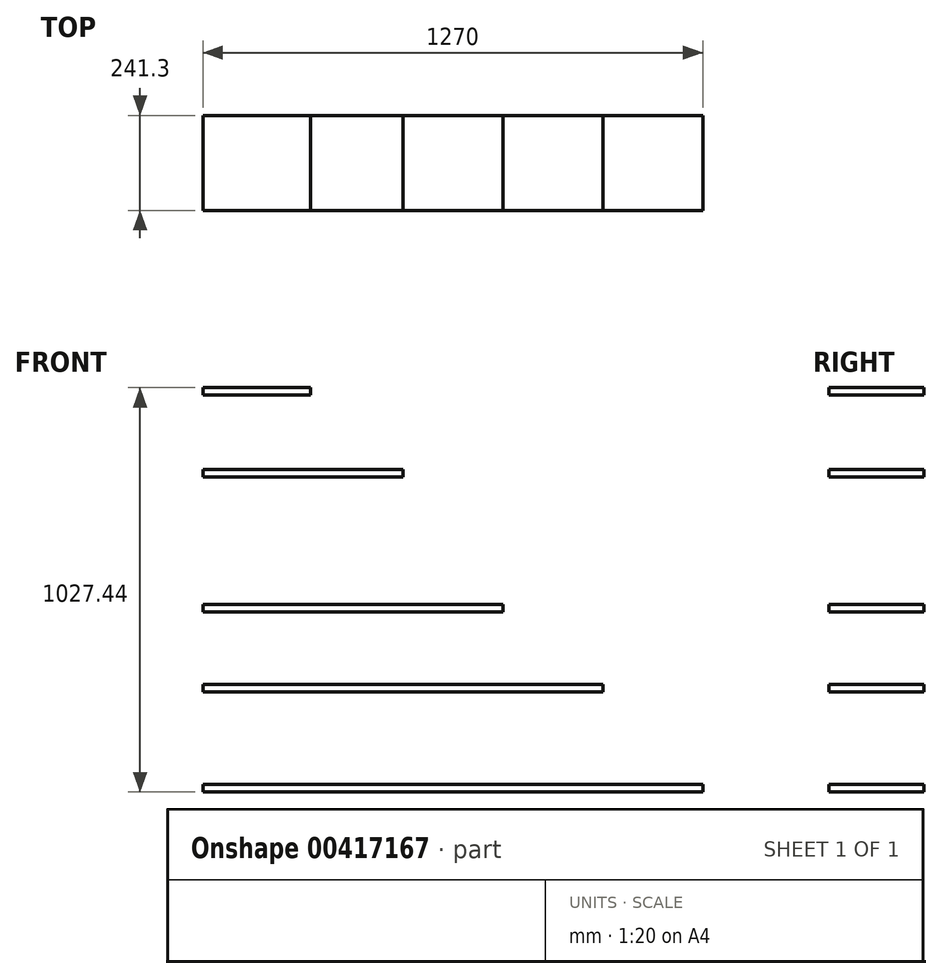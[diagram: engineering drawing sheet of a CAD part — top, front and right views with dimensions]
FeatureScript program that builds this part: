
annotation { "Feature Type Name" : "Feature", "Feature Type Description" : "" }
export const myFeature = defineFeature(function(context is Context, id is Id, definition is map)
    precondition{}
    {
        {
            var Q0;
            Q0=qCreatedBy(makeId("Front.planeOp"),FACE);
            var sketch = newSketch(context, id + "F0", { "sketchPlane" : qUnion([Q0])});
            skLineSegment(sketch, "E0.bottom", {"start": v(635, 9.52) * mm, "end": v(-635, 9.52) * mm});
            skLineSegment(sketch, "E0.top", {"start": v(635, -9.53) * mm, "end": v(-635, -9.53) * mm});
            skLineSegment(sketch, "E0.left", {"start": v(635, 9.52) * mm, "end": v(635, -9.53) * mm});
            skLineSegment(sketch, "E0.right", {"start": v(-635, 9.52) * mm, "end": v(-635, -9.53) * mm});
            skPoint(sketch, "E0.middle", {"position": v(0, 0) * mm});
            skSolve(sketch);
        }
        {
            var Q0;
            Q0 = qSketchRegion(id + "F0", true);
            extrude(context, id + "F1", {"entities" : qUnion([Q0]), "depth" : 241.3 * mm});
        }
        {
            var Q0;
            Q0=makeQuery(id+"F1.opExtrude","SWEPT_BODY",BODY,{"disambiguationData":[OSD([sQuery(id+"F0.wireOp",EDGE,"E0.bottom"),sQuery(id+"F0.wireOp",EDGE,"E0.top"),sQuery(id+"F0.wireOp",EDGE,"E0.left"),sQuery(id+"F0.wireOp",EDGE,"E0.right")])]});
            transform(context, id + "F2", {"entities" : qUnion([Q0]), "transformType" : TransformType.TRANSLATION_3D, "dx" : 0 * mm, "dy" : 0 * mm, "dz" : 254 * mm, "makeCopy" : true});
        }
        {
            var Q0;
            Q0=makeQuery(id+"F2.opPattern","COPY",FACE,{"derivedFrom":makeQuery(id+"F1.opExtrude","CAP_FACE",FACE,{"disambiguationData":[OSD([sQuery(id+"F0.wireOp",EDGE,"E0.bottom"),sQuery(id+"F0.wireOp",EDGE,"E0.top"),sQuery(id+"F0.wireOp",EDGE,"E0.left"),sQuery(id+"F0.wireOp",EDGE,"E0.right")])],"isStart":false}),"instanceName":"1"});
            var sketch = newSketch(context, id + "F3", { "sketchPlane" : qUnion([Q0])});
            skLineSegment(sketch, "E1.bottom", {"start": v(635, 263.52) * mm, "end": v(381, 263.52) * mm});
            skLineSegment(sketch, "E1.top", {"start": v(635, 244.47) * mm, "end": v(381, 244.47) * mm});
            skLineSegment(sketch, "E1.left", {"start": v(635, 263.52) * mm, "end": v(635, 244.47) * mm});
            skLineSegment(sketch, "E1.right", {"start": v(381, 263.52) * mm, "end": v(381, 244.47) * mm});
            skSolve(sketch);
        }
        {
            var Q0;
            Q0 = qSketchRegion(id + "F3", true);
            extrude(context, id + "F4", {"entities" : qUnion([Q0]), "operationType" : NewBodyOperationType.REMOVE, "endBound" : BoundingType.THROUGH_ALL, "oppositeDirection" : true, "depth" : 25.4 * mm});
        }
        {
            var Q0;
            Q0=makeQuery(id+"F2.opPattern","COPY",BODY,{"derivedFrom":makeQuery(id+"F1.opExtrude","SWEPT_BODY",BODY,{"disambiguationData":[OSD([sQuery(id+"F0.wireOp",EDGE,"E0.bottom"),sQuery(id+"F0.wireOp",EDGE,"E0.top"),sQuery(id+"F0.wireOp",EDGE,"E0.left"),sQuery(id+"F0.wireOp",EDGE,"E0.right")])]}),"instanceName":"1"});
            transform(context, id + "F5", {"entities" : qUnion([Q0]), "transformType" : TransformType.TRANSLATION_3D, "dx" : 0 * mm, "dy" : 0 * mm, "dz" : 203.2 * mm, "makeCopy" : true});
        }
        {
            var Q0;
            Q0=makeQuery(id+"F5.opPattern","COPY",FACE,{"derivedFrom":makeQuery(id+"F2.opPattern","COPY",FACE,{"derivedFrom":makeQuery(id+"F1.opExtrude","CAP_FACE",FACE,{"disambiguationData":[OSD([sQuery(id+"F0.wireOp",EDGE,"E0.bottom"),sQuery(id+"F0.wireOp",EDGE,"E0.top"),sQuery(id+"F0.wireOp",EDGE,"E0.left"),sQuery(id+"F0.wireOp",EDGE,"E0.right")])],"isStart":false}),"instanceName":"1"}),"instanceName":"1"});
            var sketch = newSketch(context, id + "F6", { "sketchPlane" : qUnion([Q0])});
            skLineSegment(sketch, "E2.bottom", {"start": v(381, 466.72) * mm, "end": v(127, 466.72) * mm});
            skLineSegment(sketch, "E2.top", {"start": v(381, 447.67) * mm, "end": v(127, 447.67) * mm});
            skLineSegment(sketch, "E2.left", {"start": v(381, 466.72) * mm, "end": v(381, 447.67) * mm});
            skLineSegment(sketch, "E2.right", {"start": v(127, 466.72) * mm, "end": v(127, 447.67) * mm});
            skSolve(sketch);
        }
        {
            var Q0;
            Q0 = qSketchRegion(id + "F6", true);
            extrude(context, id + "F7", {"entities" : qUnion([Q0]), "operationType" : NewBodyOperationType.REMOVE, "endBound" : BoundingType.THROUGH_ALL, "oppositeDirection" : true, "depth" : 25.4 * mm});
        }
        {
            var Q0;
            Q0=makeQuery(id+"F5.opPattern","COPY",BODY,{"derivedFrom":makeQuery(id+"F2.opPattern","COPY",BODY,{"derivedFrom":makeQuery(id+"F1.opExtrude","SWEPT_BODY",BODY,{"disambiguationData":[OSD([sQuery(id+"F0.wireOp",EDGE,"E0.bottom"),sQuery(id+"F0.wireOp",EDGE,"E0.top"),sQuery(id+"F0.wireOp",EDGE,"E0.left"),sQuery(id+"F0.wireOp",EDGE,"E0.right")])]}),"instanceName":"1"}),"instanceName":"1"});
            transform(context, id + "F8", {"entities" : qUnion([Q0]), "transformType" : TransformType.TRANSLATION_3D, "dx" : 0 * mm, "dy" : 0 * mm, "dz" : 342.9 * mm, "makeCopy" : true});
        }
        {
            var Q0;
            Q0=makeQuery(id+"F8.opPattern","COPY",FACE,{"derivedFrom":makeQuery(id+"F5.opPattern","COPY",FACE,{"derivedFrom":makeQuery(id+"F2.opPattern","COPY",FACE,{"derivedFrom":makeQuery(id+"F1.opExtrude","CAP_FACE",FACE,{"disambiguationData":[OSD([sQuery(id+"F0.wireOp",EDGE,"E0.bottom"),sQuery(id+"F0.wireOp",EDGE,"E0.top"),sQuery(id+"F0.wireOp",EDGE,"E0.left"),sQuery(id+"F0.wireOp",EDGE,"E0.right")])],"isStart":false}),"instanceName":"1"}),"instanceName":"1"}),"instanceName":"1"});
            var sketch = newSketch(context, id + "F9", { "sketchPlane" : qUnion([Q0])});
            skLineSegment(sketch, "E3.bottom", {"start": v(127, 809.62) * mm, "end": v(-127, 809.62) * mm});
            skLineSegment(sketch, "E3.top", {"start": v(127, 790.57) * mm, "end": v(-127, 790.57) * mm});
            skLineSegment(sketch, "E3.left", {"start": v(127, 809.62) * mm, "end": v(127, 790.57) * mm});
            skLineSegment(sketch, "E3.right", {"start": v(-127, 809.62) * mm, "end": v(-127, 790.57) * mm});
            skSolve(sketch);
        }
        {
            var Q0;
            Q0 = qSketchRegion(id + "F9", true);
            extrude(context, id + "F10", {"entities" : qUnion([Q0]), "operationType" : NewBodyOperationType.REMOVE, "endBound" : BoundingType.THROUGH_ALL, "oppositeDirection" : true, "depth" : 25.4 * mm});
        }
        {
            var Q0;
            Q0=makeQuery(id+"F8.opPattern","COPY",BODY,{"derivedFrom":makeQuery(id+"F5.opPattern","COPY",BODY,{"derivedFrom":makeQuery(id+"F2.opPattern","COPY",BODY,{"derivedFrom":makeQuery(id+"F1.opExtrude","SWEPT_BODY",BODY,{"disambiguationData":[OSD([sQuery(id+"F0.wireOp",EDGE,"E0.bottom"),sQuery(id+"F0.wireOp",EDGE,"E0.top"),sQuery(id+"F0.wireOp",EDGE,"E0.left"),sQuery(id+"F0.wireOp",EDGE,"E0.right")])]}),"instanceName":"1"}),"instanceName":"1"}),"instanceName":"1"});
            transform(context, id + "F11", {"entities" : qUnion([Q0]), "transformType" : TransformType.TRANSLATION_3D, "dx" : 0 * mm, "dy" : 0 * mm, "dz" : 208.28 * mm, "makeCopy" : true});
        }
        {
            var Q0;
            Q0=makeQuery(id+"F11.opPattern","COPY",FACE,{"derivedFrom":makeQuery(id+"F8.opPattern","COPY",FACE,{"derivedFrom":makeQuery(id+"F5.opPattern","COPY",FACE,{"derivedFrom":makeQuery(id+"F2.opPattern","COPY",FACE,{"derivedFrom":makeQuery(id+"F1.opExtrude","CAP_FACE",FACE,{"disambiguationData":[OSD([sQuery(id+"F0.wireOp",EDGE,"E0.bottom"),sQuery(id+"F0.wireOp",EDGE,"E0.top"),sQuery(id+"F0.wireOp",EDGE,"E0.left"),sQuery(id+"F0.wireOp",EDGE,"E0.right")])],"isStart":false}),"instanceName":"1"}),"instanceName":"1"}),"instanceName":"1"}),"instanceName":"1"});
            var sketch = newSketch(context, id + "F12", { "sketchPlane" : qUnion([Q0])});
            skLineSegment(sketch, "E4", {"start": v(-361.95, 998.85) * mm, "end": v(-361.95, 1017.9) * mm});
            skLineSegment(sketch, "E5", {"start": v(-361.95, 1017.9) * mm, "end": v(-127, 1017.9) * mm});
            skLineSegment(sketch, "E6", {"start": v(-127, 1017.9) * mm, "end": v(-127, 998.85) * mm});
            skLineSegment(sketch, "E7", {"start": v(-127, 998.85) * mm, "end": v(-361.95, 998.85) * mm});
            skSolve(sketch);
        }
        {
            var Q0;
            Q0 = qSketchRegion(id + "F12", true);
            extrude(context, id + "F13", {"entities" : qUnion([Q0]), "operationType" : NewBodyOperationType.REMOVE, "endBound" : BoundingType.THROUGH_ALL, "oppositeDirection" : true, "depth" : 25.4 * mm});
        }
    });
